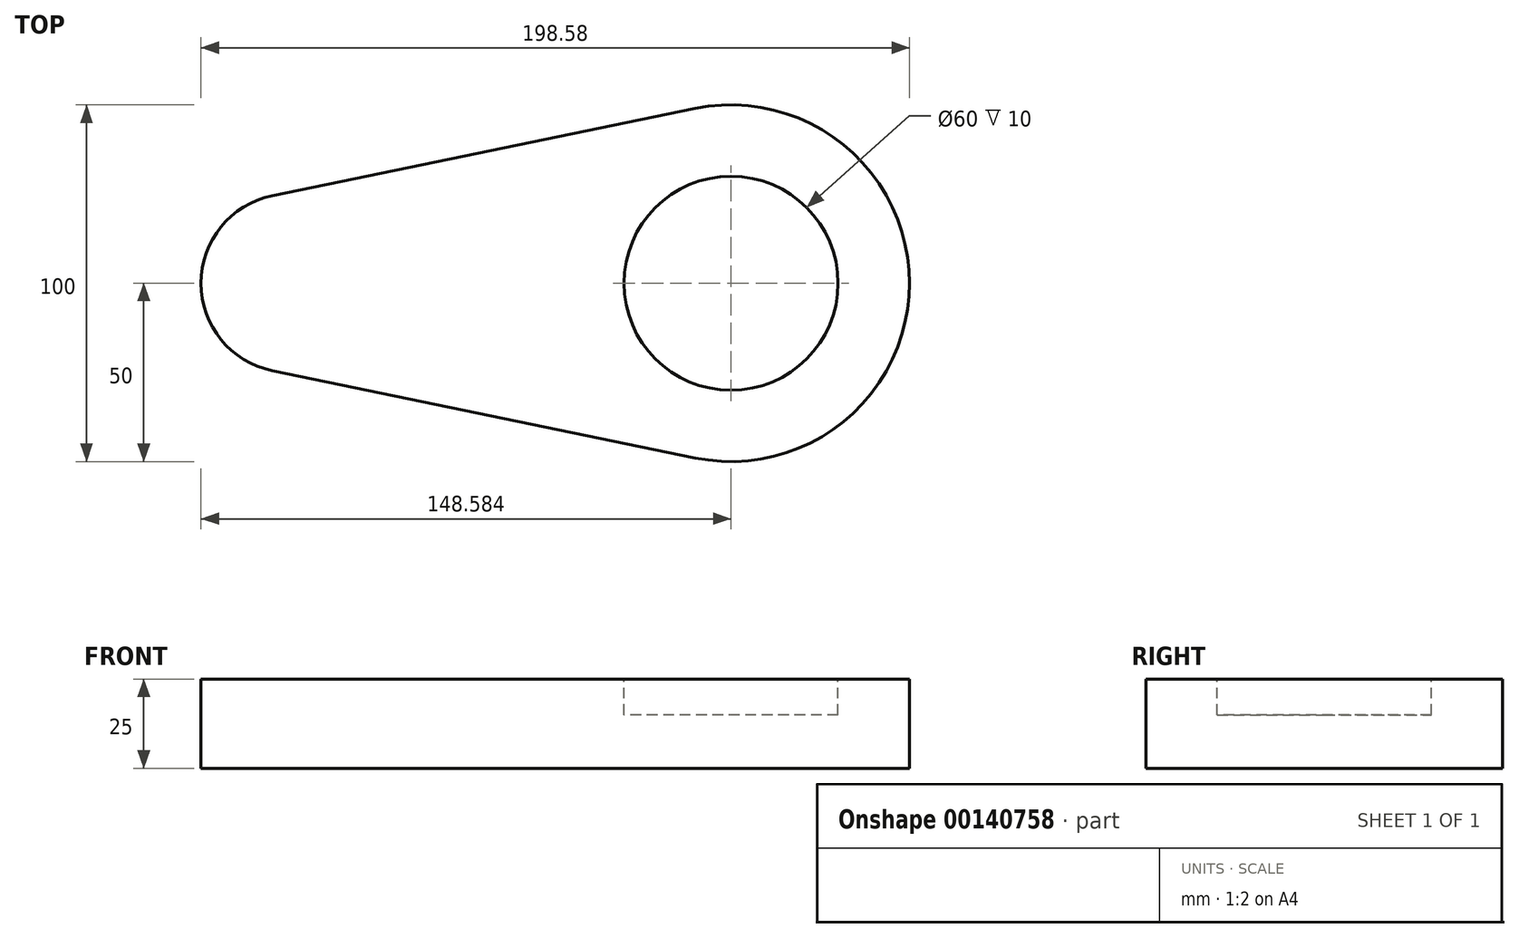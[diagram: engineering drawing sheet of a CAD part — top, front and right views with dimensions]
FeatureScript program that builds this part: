
annotation { "Feature Type Name" : "Feature", "Feature Type Description" : "" }
export const myFeature = defineFeature(function(context is Context, id is Id, definition is map)
    precondition{}
    {
        {
            var Q0;
            Q0=qCreatedBy(makeId("Top.planeOp"),FACE);
            var sketch = newSketch(context, id + "F0", { "sketchPlane" : qUnion([Q0])});
            skCircle(sketch, "E0", {"center": v(0, 0) * mm, "radius": 25 * mm});
            skCircle(sketch, "E1", {"center": v(123.58, 0) * mm, "radius": 50 * mm});
            skLineSegment(sketch, "E2", {"start": v(-5.06, -24.48) * mm, "end": v(113.47, -48.97) * mm});
            skLineSegment(sketch, "E3", {"start": v(113.47, 48.97) * mm, "end": v(-5.06, 24.48) * mm});
            skSolve(sketch);
        }
        {
            var Q0;
            Q0 = qSketchRegion(id + "F0", true);
            extrude(context, id + "F1", {"entities" : qUnion([Q0]), "depth" : 25 * mm});
        }
        {
            var Q0;
            Q0=makeQuery(id+"F1.opExtrude","CAP_FACE",FACE,{"disambiguationData":[OSD([sQuery(id+"F0.wireOp",EDGE,"E0"),sQuery(id+"F0.wireOp",EDGE,"E1"),sQuery(id+"F0.wireOp",EDGE,"E2"),sQuery(id+"F0.wireOp",EDGE,"E3")])],"isStart":false});
            var sketch = newSketch(context, id + "F2", { "sketchPlane" : qUnion([Q0])});
            skCircle(sketch, "E4", {"center": v(0, 0) * mm, "radius": 11 * mm});
            skCircle(sketch, "E5", {"center": v(123.58, 0) * mm, "radius": 30 * mm});
            skSolve(sketch);
        }
        {
            var Q0;
            Q0=makeQuery(id+"F2.imprint","IMPRINT",FACE,{"disambiguationData":[TD([[makeQuery(id+"F2.imprint","IMPRINT",EDGE,{"derivedFrom":sQuery(id+"F2.wireOp",EDGE,"E5")}),1.0]])]});
            var Q1;
            Q1=sQuery(id+"F2.wireOp",EDGE,"E5");
            extrude(context, id + "F3", {"entities" : qUnion([Q0]), "operationType" : NewBodyOperationType.REMOVE, "surfaceEntities" : qUnion([Q1]), "oppositeDirection" : true, "depth" : 10 * mm});
        }
    });
